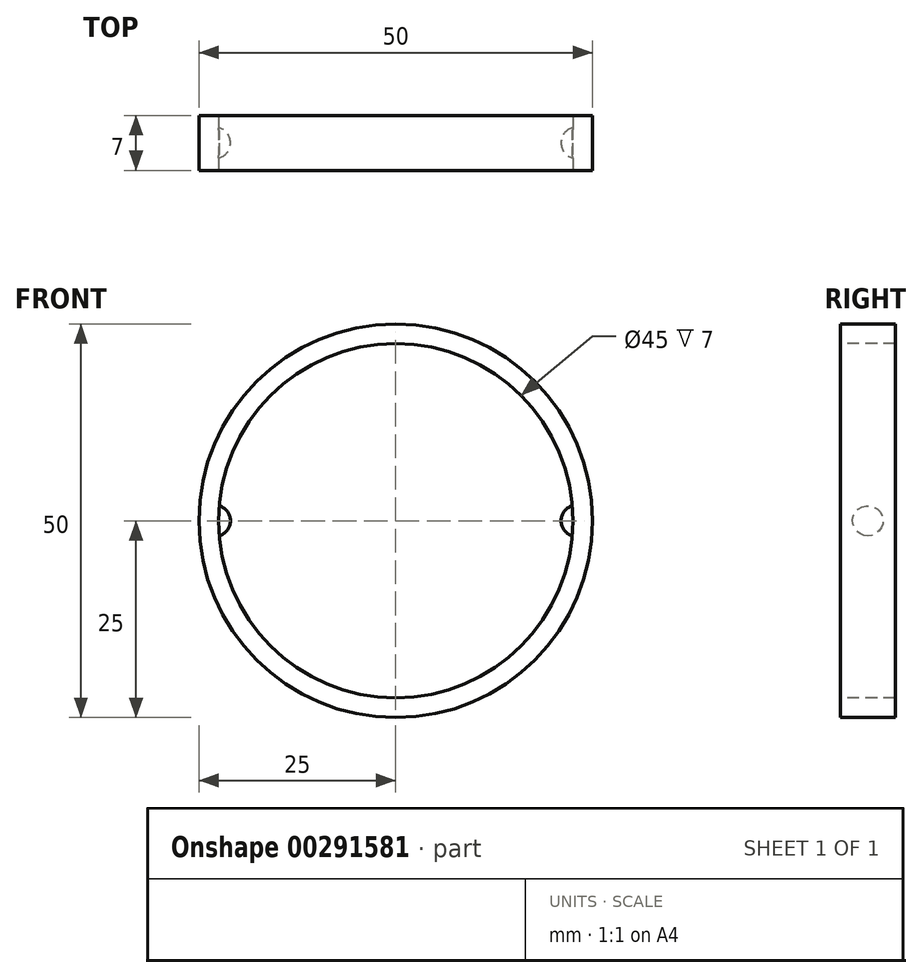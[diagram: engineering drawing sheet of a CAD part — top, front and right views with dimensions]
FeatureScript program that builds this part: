
annotation { "Feature Type Name" : "Feature", "Feature Type Description" : "" }
export const myFeature = defineFeature(function(context is Context, id is Id, definition is map)
    precondition{}
    {
        {
            var Q0;
            Q0=qCreatedBy(makeId("Front.planeOp"),FACE);
            var sketch = newSketch(context, id + "F0", { "sketchPlane" : qUnion([Q0])});
            skCircle(sketch, "E0", {"center": v(0, 0) * mm, "radius": 25 * mm});
            skSolve(sketch);
        }
        {
            var Q0;
            Q0=makeQuery(id+"F0.imprint","IMPRINT",FACE,{"disambiguationData":[TD([[makeQuery(id+"F0.imprint","IMPRINT",EDGE,{"derivedFrom":sQuery(id+"F0.wireOp",EDGE,"E0")}),1.0]])]});
            extrude(context, id + "F1", {"entities" : qUnion([Q0]), "depth" : 7 * mm});
        }
        {
            var Q0;
            Q0=makeQuery(id+"F1.opExtrude","CAP_FACE",FACE,{"disambiguationData":[OSD([sQuery(id+"F0.wireOp",EDGE,"E0")])],"isStart":false});
            var sketch = newSketch(context, id + "F2", { "sketchPlane" : qUnion([Q0])});
            skCircle(sketch, "E1", {"center": v(0, 0) * mm, "radius": 22.5 * mm});
            skSolve(sketch);
        }
        {
            var Q0;
            Q0=makeQuery(id+"F2.imprint","IMPRINT",FACE,{"disambiguationData":[TD([[makeQuery(id+"F2.imprint","IMPRINT",EDGE,{"derivedFrom":sQuery(id+"F2.wireOp",EDGE,"E1")}),1.0]])]});
            extrude(context, id + "F3", {"entities" : qUnion([Q0]), "operationType" : NewBodyOperationType.REMOVE, "oppositeDirection" : true, "depth" : 25 * mm});
        }
        {
            var Q0;
            Q0=qCreatedBy(makeId("Right.planeOp"),FACE);
            cPlane(context, id + "F4", {"entities" : qUnion([Q0]), "cplaneType" : CPlaneType.OFFSET, "offset" : 23 * mm, "width" : 150 * mm, "height" : 150 * mm});
        }
        {
            var Q0;
            Q0=qCreatedBy(id+"F4.planeOp",FACE);
            var sketch = newSketch(context, id + "F5", { "sketchPlane" : qUnion([Q0])});
            skArc(sketch, "E2", {"start": v(-1.5, 0) * mm, "mid": v(-3.5, 2) * mm, "end": v(-5.5, 0) * mm});
            skLineSegment(sketch, "E3", {"start": v(-7.1, 0) * mm, "end": v(0, 0) * mm});
            skSolve(sketch);
        }
        {
            var Q0;
            Q0 = qSketchRegion(id + "F5", true);
            var Q1;
            Q1=sQuery(id+"F5.wireOp",EDGE,"E3");
            revolve(context, id + "F6", {"operationType" : NewBodyOperationType.ADD, "entities" : qUnion([Q0]), "axis" : qUnion([Q1]), "revolveType" : RevolveType.FULL});
        }
        {
            var Q0;
            Q0=makeQuery(id+"F1.opExtrude","SWEPT_BODY",BODY,{"disambiguationData":[OSD([sQuery(id+"F0.wireOp",EDGE,"E0")])]});
            var Q1;
            Q1=qCreatedBy(makeId("Right.planeOp"),FACE);
            mirror(context, id + "F7", {"operationType" : NewBodyOperationType.ADD, "entities" : qUnion([Q0]), "mirrorPlane" : qUnion([Q1])});
        }
    });
